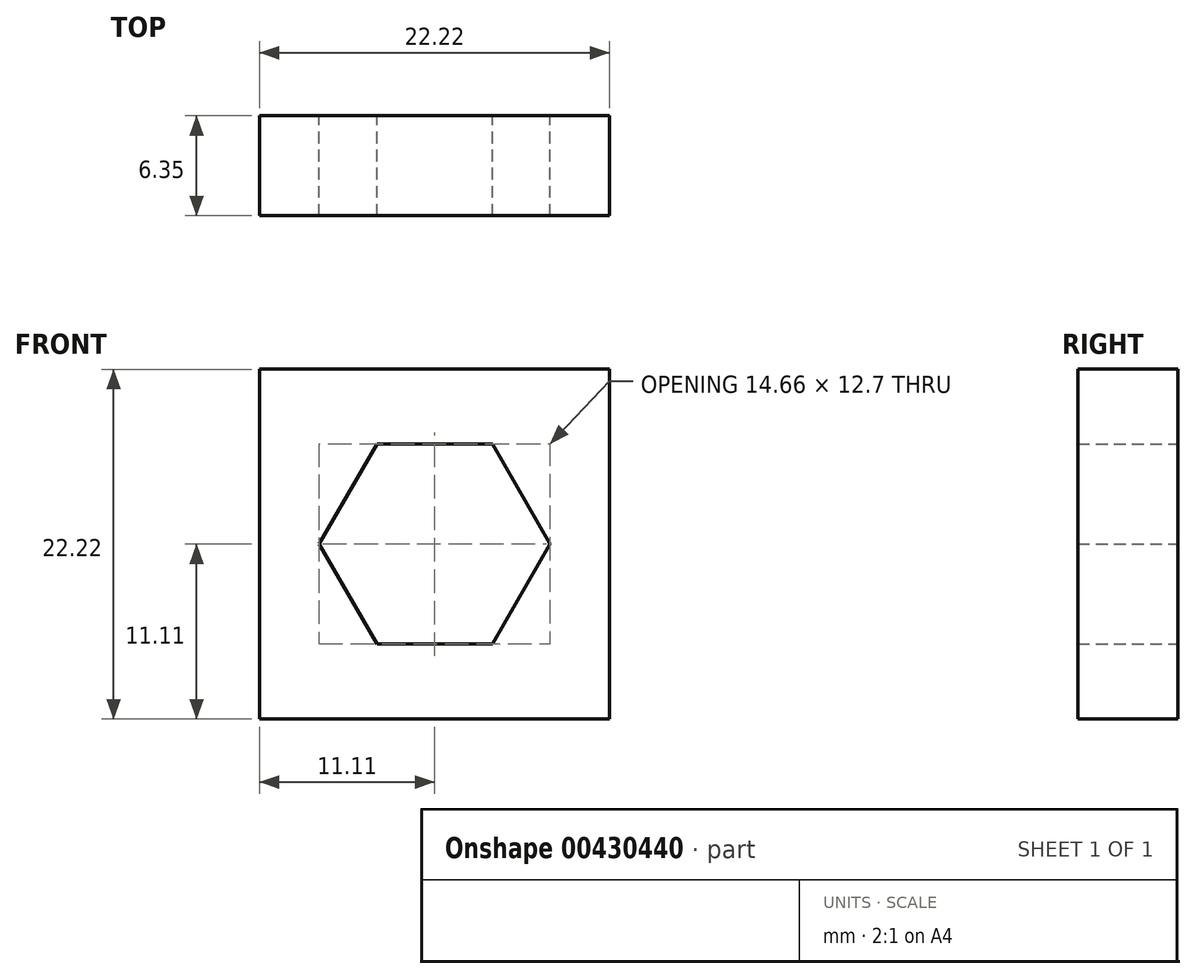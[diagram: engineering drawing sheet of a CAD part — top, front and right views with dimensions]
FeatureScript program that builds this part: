
annotation { "Feature Type Name" : "Feature", "Feature Type Description" : "" }
export const myFeature = defineFeature(function(context is Context, id is Id, definition is map)
    precondition{}
    {
        {
            var Q0;
            Q0=qCreatedBy(makeId("Front.planeOp"),FACE);
            var sketch = newSketch(context, id + "F0", { "sketchPlane" : qUnion([Q0])});
            skLineSegment(sketch, "E0.bottom", {"start": v(-11.11, 11.11) * mm, "end": v(11.11, 11.11) * mm});
            skLineSegment(sketch, "E0.top", {"start": v(-11.11, -11.11) * mm, "end": v(11.11, -11.11) * mm});
            skLineSegment(sketch, "E0.left", {"start": v(-11.11, 11.11) * mm, "end": v(-11.11, -11.11) * mm});
            skLineSegment(sketch, "E0.right", {"start": v(11.11, 11.11) * mm, "end": v(11.11, -11.11) * mm});
            skPoint(sketch, "E0.middle", {"position": v(0, 0) * mm});
            skCircle(sketch, "E1.cCircle", {"center": v(0, 0) * mm, "radius": 6.35 * mm, "construction": true});
            skLineSegment(sketch, "E1.0", {"start": v(-3.67, 6.35) * mm, "end": v(3.67, 6.35) * mm});
            skLineSegment(sketch, "E1.1", {"start": v(3.67, 6.35) * mm, "end": v(7.33, 0) * mm});
            skLineSegment(sketch, "E1.2", {"start": v(7.33, 0) * mm, "end": v(3.67, -6.35) * mm});
            skLineSegment(sketch, "E1.3", {"start": v(3.67, -6.35) * mm, "end": v(-3.67, -6.35) * mm});
            skLineSegment(sketch, "E1.4", {"start": v(-3.67, -6.35) * mm, "end": v(-7.33, 0) * mm});
            skLineSegment(sketch, "E1.5", {"start": v(-7.33, 0) * mm, "end": v(-3.67, 6.35) * mm});
            skPoint(sketch, "E1.0.midPoint", {"position": v(0, 6.35) * mm});
            skSolve(sketch);
        }
        {
            var Q0;
            Q0 = qSketchRegion(id + "F0", true);
            extrude(context, id + "F1", {"entities" : qUnion([Q0]), "depth" : 6.35 * mm});
        }
    });
